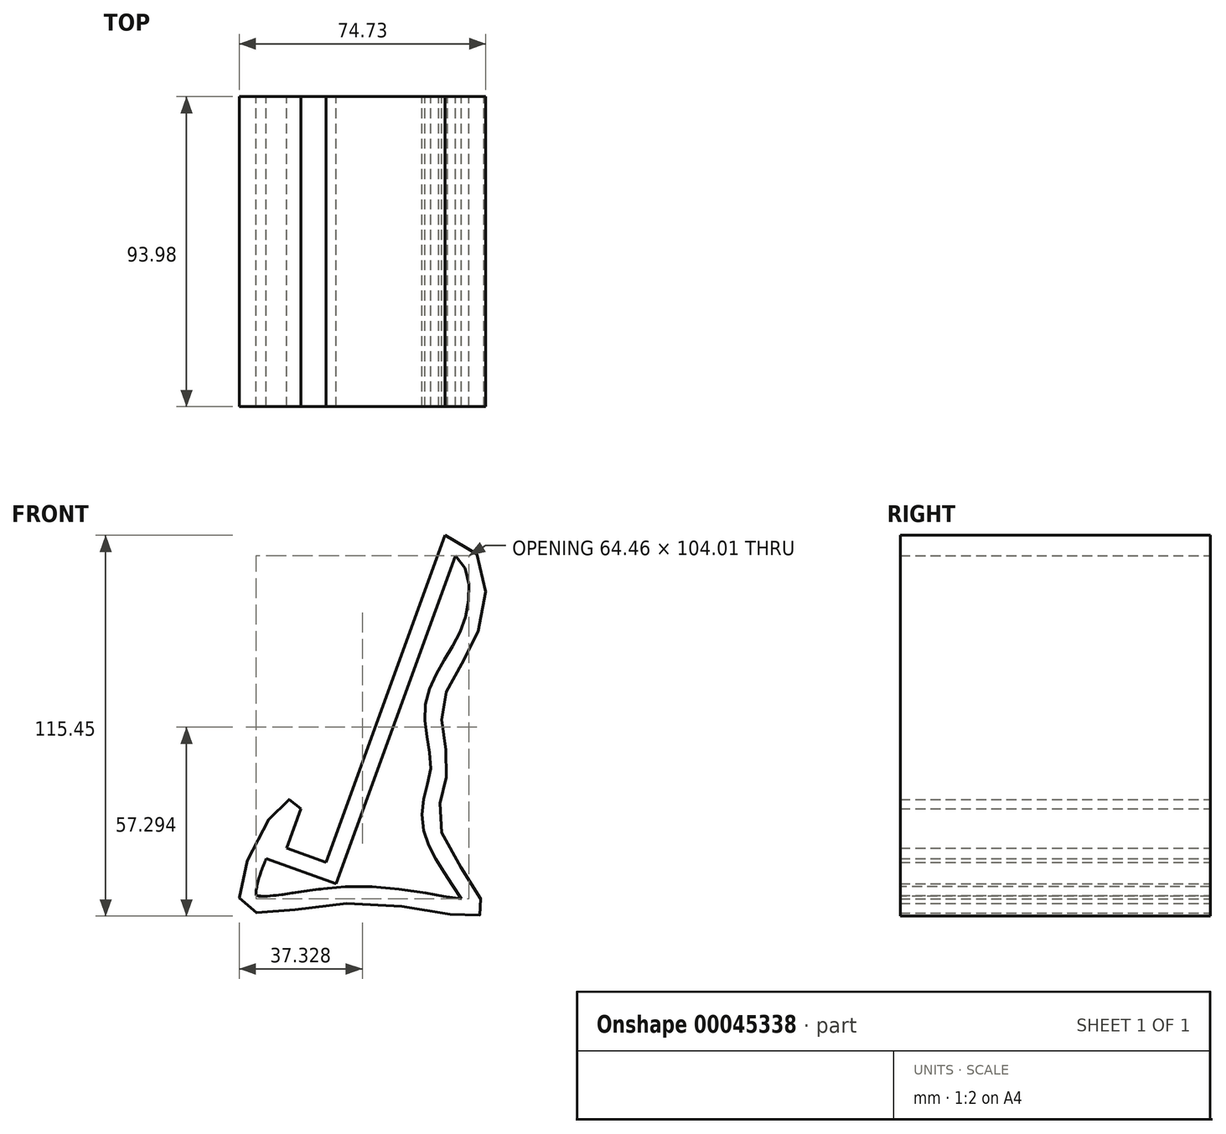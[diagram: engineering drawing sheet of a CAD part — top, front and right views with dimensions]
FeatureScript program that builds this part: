
annotation { "Feature Type Name" : "Feature", "Feature Type Description" : "" }
export const myFeature = defineFeature(function(context is Context, id is Id, definition is map)
    precondition{}
    {
        {
            var Q0;
            Q0=qCreatedBy(makeId("Front.planeOp"),FACE);
            var sketch = newSketch(context, id + "F0", { "sketchPlane" : qUnion([Q0])});
            skLineSegment(sketch, "E0.bottom", {"start": v(0, 0) * mm, "end": v(101.6, 0) * mm, "construction": true});
            skLineSegment(sketch, "E0.top", {"start": v(0, 152.4) * mm, "end": v(101.6, 152.4) * mm, "construction": true});
            skLineSegment(sketch, "E0.left", {"start": v(0, 0) * mm, "end": v(0, 152.4) * mm, "construction": true});
            skLineSegment(sketch, "E0.right", {"start": v(101.6, 0) * mm, "end": v(101.6, 152.4) * mm, "construction": true});
            skLineSegment(sketch, "E1", {"start": v(11.93, 53.24) * mm, "end": v(48.02, 152.4) * mm});
            skLineSegment(sketch, "E2", {"start": v(11.93, 53.24) * mm, "end": v(0, 57.59) * mm});
            skLineSegment(sketch, "E3", {"start": v(0, 57.59) * mm, "end": v(4.34, 69.52) * mm});
            skFitSpline(sketch, "E4", {"points": [v(4.34, 69.52) * mm, v(0, 72.07) * mm, v(-14.05, 41.38) * mm, v(21.03, 40.86) * mm, v(59.8, 38.4) * mm, v(46.86, 62.86) * mm, v(48.74, 81.2) * mm, v(47.33, 101.47) * mm, v(59.09, 126.13) * mm, v(48.02, 152.4) * mm], "startDerivative": vector(-67.22, 102.98) * mm, "endDerivative": vector(-315.4, 25.3) * mm});
            skSolve(sketch);
        }
        {
            var Q0;
            Q0=makeQuery(id+"F0.imprint","IMPRINT",FACE,{"disambiguationData":[TD([[makeQuery(id+"F0.imprint","IMPRINT",EDGE,{"derivedFrom":sQuery(id+"F0.wireOp",EDGE,"E1")}),-1.0]])]});
            extrude(context, id + "F1", {"entities" : qUnion([Q0]), "depth" : 93.98 * mm});
        }
        {
            var Q0;
            Q0=makeQuery(id+"F1.opExtrude","CAP_FACE",FACE,{"disambiguationData":[OSD([sQuery(id+"F0.wireOp",EDGE,"E1"),sQuery(id+"F0.wireOp",EDGE,"E2"),sQuery(id+"F0.wireOp",EDGE,"E3"),sQuery(id+"F0.wireOp",EDGE,"E4")])],"isStart":true});
            var Q1;
            Q1=makeQuery(id+"F1.opExtrude","CAP_FACE",FACE,{"disambiguationData":[OSD([sQuery(id+"F0.wireOp",EDGE,"E1"),sQuery(id+"F0.wireOp",EDGE,"E2"),sQuery(id+"F0.wireOp",EDGE,"E3"),sQuery(id+"F0.wireOp",EDGE,"E4")])],"isStart":false});
            shell(context, id + "F2", {"entities" : qUnion([Q0, Q1]), "thickness" : 5.08 * mm});
        }
    });
